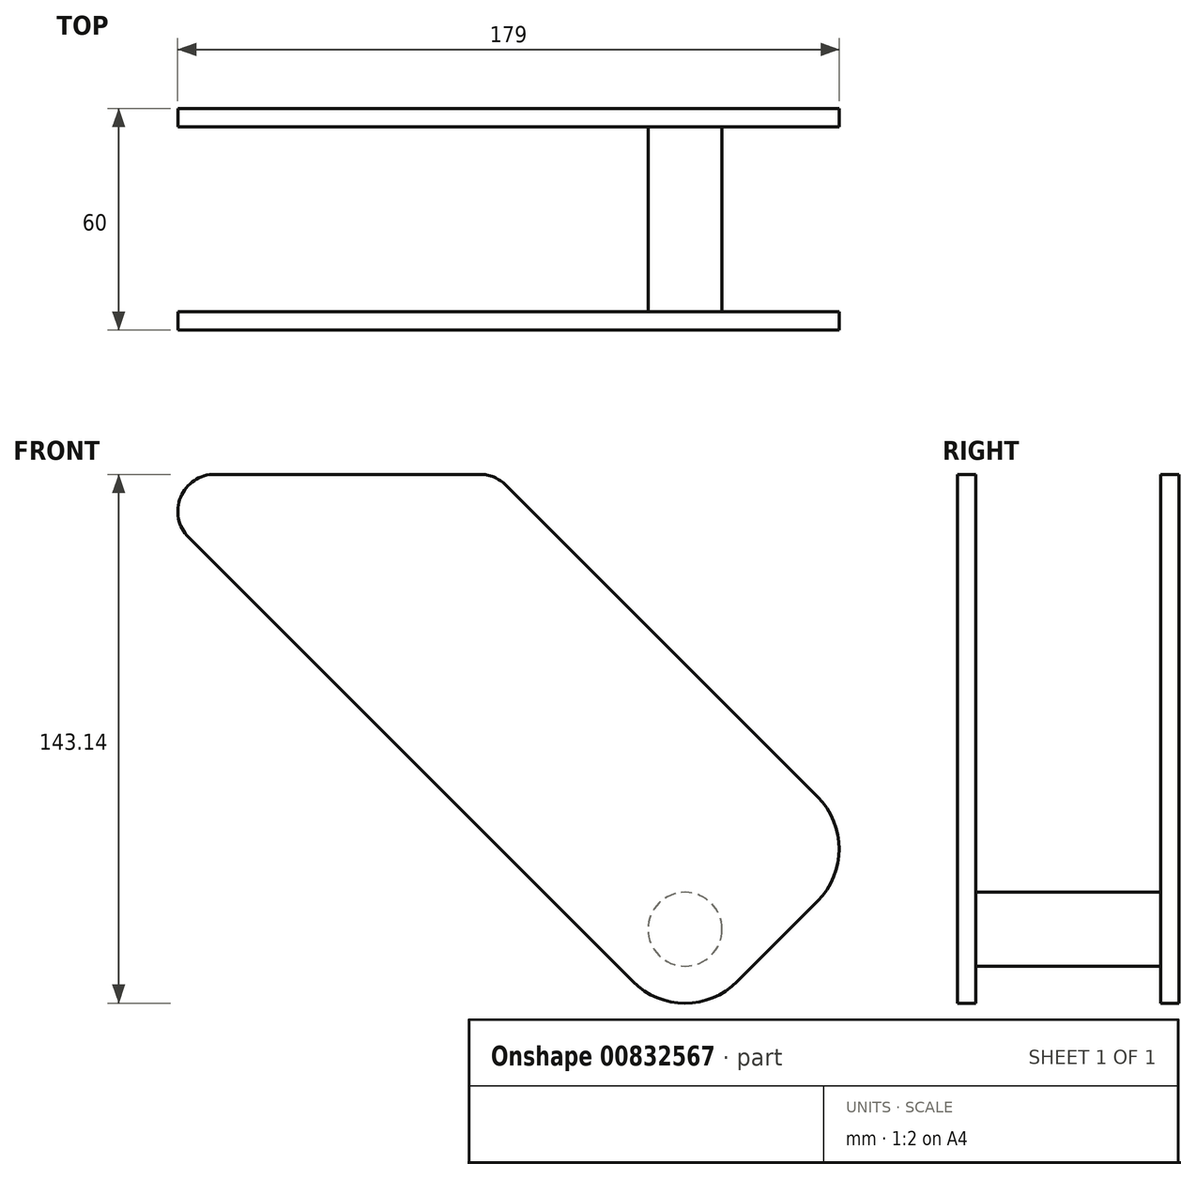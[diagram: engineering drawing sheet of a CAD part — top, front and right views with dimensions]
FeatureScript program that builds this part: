
annotation { "Feature Type Name" : "Feature", "Feature Type Description" : "" }
export const myFeature = defineFeature(function(context is Context, id is Id, definition is map)
    precondition{}
    {
        {
            var Q0;
            Q0=qCreatedBy(makeId("Front.planeOp"),FACE);
            cPlane(context, id + "F0", {"entities" : qUnion([Q0]), "cplaneType" : CPlaneType.OFFSET, "offset" : 25 * mm, "width" : 150 * mm, "height" : 150 * mm});
        }
        {
            var Q0;
            Q0=qCreatedBy(id+"F0.planeOp",FACE);
            var sketch = newSketch(context, id + "F1", { "sketchPlane" : qUnion([Q0])});
            skLineSegment(sketch, "E0.bottom", {"start": v(-75.86, 50) * mm, "end": v(-4.14, 50) * mm});
            skLineSegment(sketch, "E1", {"start": v(65.56, -87.28) * mm, "end": v(87.28, -65.56) * mm});
            skLineSegment(sketch, "E2", {"start": v(87.28, -37.28) * mm, "end": v(2.93, 47.07) * mm});
            skLineSegment(sketch, "E3", {"start": v(37.28, -87.28) * mm, "end": v(-82.93, 32.93) * mm});
            skPoint(sketch, "E4.orphan", {"position": v(-99.24, 50) * mm});
            skPoint(sketch, "E5.orphan", {"position": v(99.24, 50) * mm});
            skPoint(sketch, "E6.orphan", {"position": v(103.6, -152.84) * mm});
            skPoint(sketch, "E0.left.end.orphan", {"position": v(-0.76, -50) * mm});
            skPoint(sketch, "E7.visualSharp", {"position": v(-100, 50) * mm});
            skArc(sketch, "E7.filletArc", {"start": v(-75.86, 50) * mm, "mid": v(-85.1, 43.83) * mm, "end": v(-82.93, 32.93) * mm});
            skPoint(sketch, "E8.visualSharp", {"position": v(0, 50) * mm});
            skArc(sketch, "E8.filletArc", {"start": v(2.93, 47.07) * mm, "mid": v(-0.32, 49.24) * mm, "end": v(-4.14, 50) * mm});
            skPoint(sketch, "E9.visualSharp", {"position": v(101.42, -51.42) * mm});
            skArc(sketch, "E9.filletArc", {"start": v(87.28, -65.56) * mm, "mid": v(93.14, -51.42) * mm, "end": v(87.28, -37.28) * mm});
            skPoint(sketch, "E10.visualSharp", {"position": v(51.42, -101.42) * mm});
            skArc(sketch, "E10.filletArc", {"start": v(37.28, -87.28) * mm, "mid": v(51.42, -93.14) * mm, "end": v(65.56, -87.28) * mm});
            skSolve(sketch);
        }
        {
            var Q0;
            Q0=makeQuery(id+"F1.imprint","IMPRINT",FACE,{"disambiguationData":[TD([[makeQuery(id+"F1.imprint","IMPRINT",EDGE,{"derivedFrom":sQuery(id+"F1.wireOp",EDGE,"E0.bottom")}),-1.0]])]});
            extrude(context, id + "F2", {"entities" : qUnion([Q0]), "depth" : 5 * mm, "offsetDistance" : 25 * mm});
        }
        {
            var Q0;
            Q0=makeQuery(id+"F2.opExtrude","CAP_FACE",FACE,{"disambiguationData":[OSD([sQuery(id+"F1.wireOp",EDGE,"E0.bottom"),sQuery(id+"F1.wireOp",EDGE,"E1"),sQuery(id+"F1.wireOp",EDGE,"E2"),sQuery(id+"F1.wireOp",EDGE,"E3"),sQuery(id+"F1.wireOp",EDGE,"E7.filletArc"),sQuery(id+"F1.wireOp",EDGE,"E8.filletArc"),sQuery(id+"F1.wireOp",EDGE,"E9.filletArc"),sQuery(id+"F1.wireOp",EDGE,"E10.filletArc")])],"isStart":true});
            var sketch = newSketch(context, id + "F3", { "sketchPlane" : qUnion([Q0])});
            skCircle(sketch, "E11", {"center": v(-51.42, -73.14) * mm, "radius": 10 * mm});
            skSolve(sketch);
        }
        {
            var Q0;
            Q0=makeQuery(id+"F3.imprint","IMPRINT",FACE,{"disambiguationData":[TD([[makeQuery(id+"F3.imprint","IMPRINT",EDGE,{"derivedFrom":sQuery(id+"F3.wireOp",EDGE,"E11")}),1.0]])]});
            extrude(context, id + "F4", {"entities" : qUnion([Q0]), "operationType" : NewBodyOperationType.ADD, "depth" : 25 * mm, "offsetDistance" : 25 * mm});
        }
        {
            var Q0;
            Q0=makeQuery(id+"F2.opExtrude","SWEPT_BODY",BODY,{"disambiguationData":[OSD([sQuery(id+"F1.wireOp",EDGE,"E0.bottom"),sQuery(id+"F1.wireOp",EDGE,"E1"),sQuery(id+"F1.wireOp",EDGE,"E2"),sQuery(id+"F1.wireOp",EDGE,"E3"),sQuery(id+"F1.wireOp",EDGE,"E7.filletArc"),sQuery(id+"F1.wireOp",EDGE,"E8.filletArc"),sQuery(id+"F1.wireOp",EDGE,"E9.filletArc"),sQuery(id+"F1.wireOp",EDGE,"E10.filletArc")])]});
            var Q1;
            Q1=qCreatedBy(makeId("Front.planeOp"),FACE);
            mirror(context, id + "F5", {"operationType" : NewBodyOperationType.ADD, "entities" : qUnion([Q0]), "mirrorPlane" : qUnion([Q1])});
        }
    });
